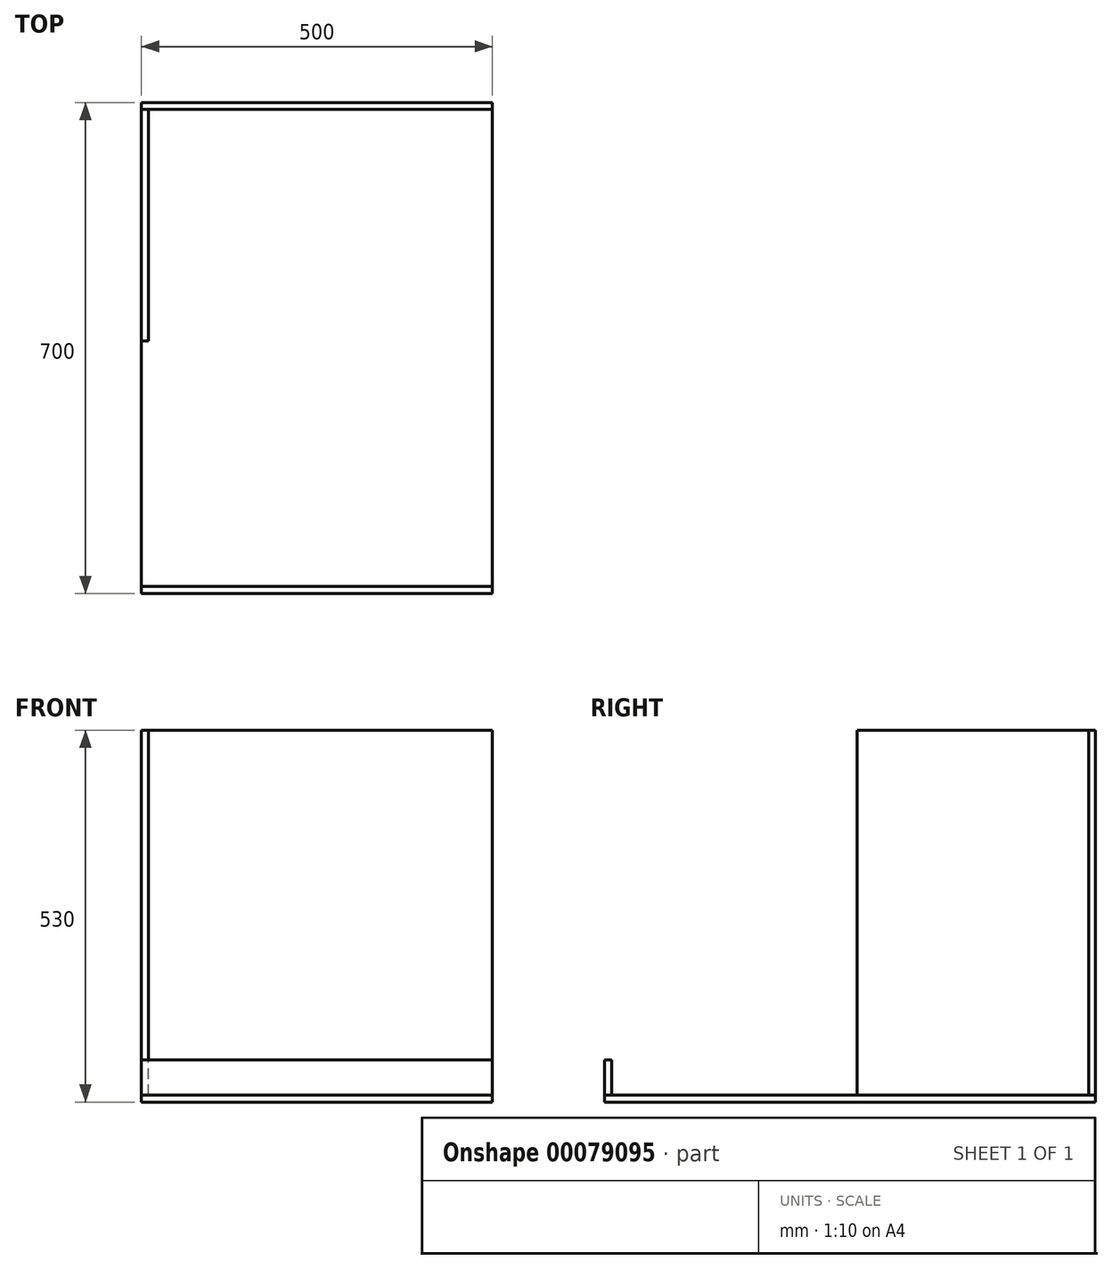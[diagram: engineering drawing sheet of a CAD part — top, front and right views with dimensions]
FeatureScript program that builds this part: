
annotation { "Feature Type Name" : "Feature", "Feature Type Description" : "" }
export const myFeature = defineFeature(function(context is Context, id is Id, definition is map)
    precondition{}
    {
        {
            assignVariable(context, id + "F0", {"name" : "wall", "anyValue" : 10});
        }
        {
            var Q0;
            Q0=qCreatedBy(makeId("Top.planeOp"),FACE);
            var sketch = newSketch(context, id + "F1", { "sketchPlane" : qUnion([Q0])});
            skLineSegment(sketch, "E0.bottom", {"start": v(250, -350) * mm, "end": v(-250, -350) * mm});
            skLineSegment(sketch, "E0.top", {"start": v(250, 350) * mm, "end": v(-250, 350) * mm});
            skLineSegment(sketch, "E0.left", {"start": v(250, -350) * mm, "end": v(250, 350) * mm});
            skLineSegment(sketch, "E0.right", {"start": v(-250, -350) * mm, "end": v(-250, 350) * mm});
            skPoint(sketch, "E0.middle", {"position": v(0, 0) * mm});
            skSolve(sketch);
        }
        {
            var Q0;
            Q0 = qSketchRegion(id + "F1", true);
            extrude(context, id + "F2", {"entities" : qUnion([Q0]), "depth" : (getVariable(context, 'wall')) * mm});
        }
        {
            var Q0;
            Q0=makeQuery(id+"F2.opExtrude","SWEPT_FACE",FACE,{"disambiguationData":[OSD([sQuery(id+"F1.wireOp",EDGE,"E0.top")])]});
            var sketch = newSketch(context, id + "F3", { "sketchPlane" : qUnion([Q0])});
            skLineSegment(sketch, "E1.bottom", {"start": v(250, 10) * mm, "end": v(-250, 10) * mm});
            skLineSegment(sketch, "E1.top", {"start": v(250, 530) * mm, "end": v(-250, 530) * mm});
            skLineSegment(sketch, "E1.left", {"start": v(250, 10) * mm, "end": v(250, 530) * mm});
            skLineSegment(sketch, "E1.right", {"start": v(-250, 10) * mm, "end": v(-250, 530) * mm});
            skPoint(sketch, "E1.middle", {"position": v(0, 270) * mm});
            skSolve(sketch);
        }
        {
            var Q0;
            Q0 = qSketchRegion(id + "F3", true);
            extrude(context, id + "F4", {"entities" : qUnion([Q0]), "oppositeDirection" : true, "depth" : (getVariable(context, 'wall')) * mm});
        }
        {
            var Q0;
            Q0=makeQuery(id+"F2.opExtrude","SWEPT_FACE",FACE,{"disambiguationData":[OSD([sQuery(id+"F1.wireOp",EDGE,"E0.right")])]});
            var sketch = newSketch(context, id + "F5", { "sketchPlane" : qUnion([Q0])});
            skLineSegment(sketch, "E2.bottom", {"start": v(-340, 10) * mm, "end": v(-10, 10) * mm});
            skLineSegment(sketch, "E2.top", {"start": v(-340, 530) * mm, "end": v(-10, 530) * mm});
            skLineSegment(sketch, "E2.left", {"start": v(-340, 10) * mm, "end": v(-340, 530) * mm});
            skLineSegment(sketch, "E2.right", {"start": v(-10, 10) * mm, "end": v(-10, 530) * mm});
            skSolve(sketch);
        }
        {
            var Q0;
            Q0 = qSketchRegion(id + "F5", true);
            extrude(context, id + "F6", {"entities" : qUnion([Q0]), "oppositeDirection" : true, "depth" : (getVariable(context, 'wall')) * mm});
        }
        {
            var Q0;
            Q0=makeQuery(id+"F2.opExtrude","SWEPT_FACE",FACE,{"disambiguationData":[OSD([sQuery(id+"F1.wireOp",EDGE,"E0.bottom")])]});
            var sketch = newSketch(context, id + "F7", { "sketchPlane" : qUnion([Q0])});
            skLineSegment(sketch, "E3.bottom", {"start": v(-250, 10) * mm, "end": v(250, 10) * mm});
            skLineSegment(sketch, "E3.top", {"start": v(-250, 60) * mm, "end": v(250, 60) * mm});
            skLineSegment(sketch, "E3.left", {"start": v(-250, 10) * mm, "end": v(-250, 60) * mm});
            skLineSegment(sketch, "E3.right", {"start": v(250, 10) * mm, "end": v(250, 60) * mm});
            skSolve(sketch);
        }
        {
            var Q0;
            Q0 = qSketchRegion(id + "F7", true);
            extrude(context, id + "F8", {"entities" : qUnion([Q0]), "oppositeDirection" : true, "depth" : (getVariable(context, 'wall')) * mm});
        }
    });
